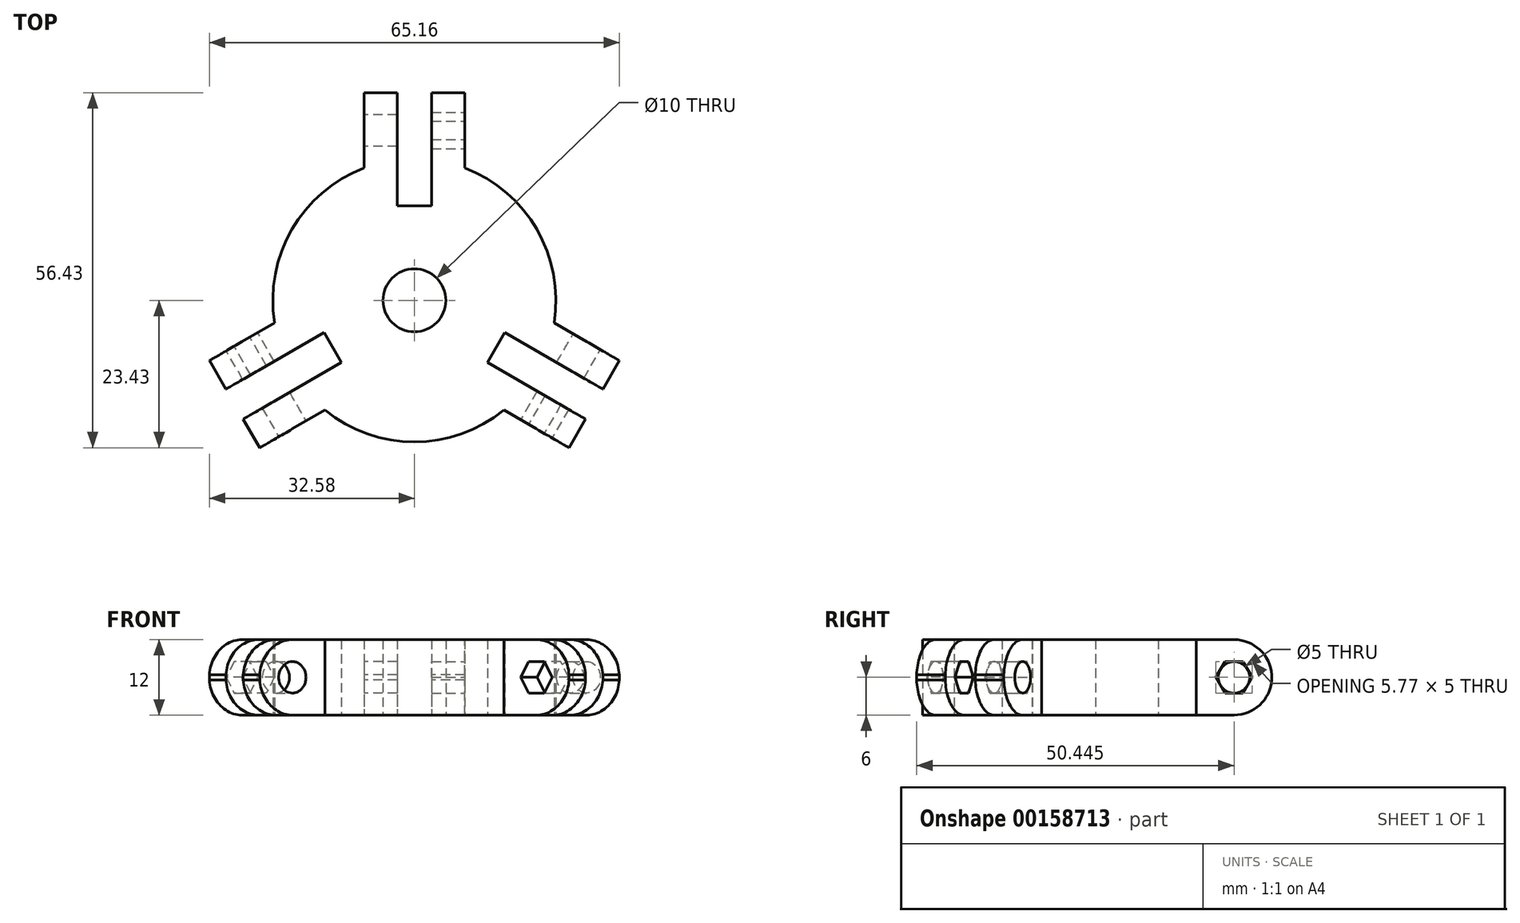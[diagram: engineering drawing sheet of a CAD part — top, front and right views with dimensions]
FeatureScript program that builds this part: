
annotation { "Feature Type Name" : "Feature", "Feature Type Description" : "" }
export const myFeature = defineFeature(function(context is Context, id is Id, definition is map)
    precondition{}
    {
        {
            var Q0;
            Q0=qCreatedBy(makeId("Top.planeOp"),FACE);
            var sketch = newSketch(context, id + "F0", { "sketchPlane" : qUnion([Q0])});
            skCircle(sketch, "E0", {"center": v(0, 0) * mm, "radius": 5 * mm});
            skLineSegment(sketch, "E1", {"start": v(0, 15) * mm, "end": v(2.75, 15) * mm});
            skLineSegment(sketch, "E2", {"start": v(2.75, 15) * mm, "end": v(2.75, 33) * mm});
            skLineSegment(sketch, "E3", {"start": v(2.75, 33) * mm, "end": v(8, 33) * mm});
            skLineSegment(sketch, "E4", {"start": v(0, 15) * mm, "end": v(-2.75, 15) * mm});
            skLineSegment(sketch, "E5", {"start": v(-2.75, 15) * mm, "end": v(-2.75, 33) * mm});
            skLineSegment(sketch, "E6", {"start": v(-2.75, 33) * mm, "end": v(-8, 33) * mm});
            skLineSegment(sketch, "E7", {"start": v(0, 0) * mm, "end": v(13, -7.5) * mm});
            skLineSegment(sketch, "E8", {"start": v(0, 0) * mm, "end": v(-13, -7.5) * mm});
            skLineSegment(sketch, "E9", {"start": v(-13, -7.5) * mm, "end": v(-14.37, -5.12) * mm});
            skLineSegment(sketch, "E10", {"start": v(-14.37, -5.12) * mm, "end": v(-29.95, -14.12) * mm});
            skLineSegment(sketch, "E11", {"start": v(-29.95, -14.12) * mm, "end": v(-32.58, -9.57) * mm});
            skLineSegment(sketch, "E12", {"start": v(-13, -7.5) * mm, "end": v(-11.62, -9.88) * mm});
            skLineSegment(sketch, "E13", {"start": v(-11.62, -9.88) * mm, "end": v(-27.2, -18.88) * mm});
            skLineSegment(sketch, "E14", {"start": v(-27.2, -18.88) * mm, "end": v(-24.58, -23.43) * mm});
            skLineSegment(sketch, "E15", {"start": v(13, -7.5) * mm, "end": v(14.37, -5.12) * mm});
            skLineSegment(sketch, "E16", {"start": v(14.37, -5.12) * mm, "end": v(29.95, -14.12) * mm});
            skLineSegment(sketch, "E17", {"start": v(29.95, -14.12) * mm, "end": v(32.58, -9.57) * mm});
            skLineSegment(sketch, "E18", {"start": v(13, -7.5) * mm, "end": v(11.62, -9.88) * mm});
            skLineSegment(sketch, "E19", {"start": v(11.62, -9.88) * mm, "end": v(27.2, -18.88) * mm});
            skLineSegment(sketch, "E20", {"start": v(27.2, -18.88) * mm, "end": v(24.58, -23.43) * mm});
            skPoint(sketch, "E21.endSnap0", {"position": v(5.37, 33) * mm});
            skArc(sketch, "E22", {"start": v(-8, 21.03) * mm, "mid": v(-19.49, 11.25) * mm, "end": v(-22.21, -3.59) * mm});
            skArc(sketch, "E23", {"start": v(8, 21.03) * mm, "mid": v(19.49, 11.25) * mm, "end": v(22.21, -3.59) * mm});
            skArc(sketch, "E24", {"start": v(-14.21, -17.44) * mm, "mid": v(0, -22.5) * mm, "end": v(14.21, -17.44) * mm});
            skLineSegment(sketch, "E25", {"start": v(-14.21, -17.44) * mm, "end": v(-24.58, -23.43) * mm});
            skLineSegment(sketch, "E26", {"start": v(-22.21, -3.59) * mm, "end": v(-32.58, -9.57) * mm});
            skLineSegment(sketch, "E27", {"start": v(-8, 21.03) * mm, "end": v(-8, 33) * mm});
            skLineSegment(sketch, "E28", {"start": v(8, 33) * mm, "end": v(8, 21.03) * mm});
            skLineSegment(sketch, "E29", {"start": v(22.21, -3.59) * mm, "end": v(32.58, -9.57) * mm});
            skLineSegment(sketch, "E30", {"start": v(24.58, -23.43) * mm, "end": v(14.21, -17.44) * mm});
            skLineSegment(sketch, "E31", {"start": v(0, 15) * mm, "end": v(0, 0) * mm});
            skSolve(sketch);
        }
        {
            var Q0;
            Q0 = qSketchRegion(id + "F0", true);
            var Q1;
            {var subQ6=sQuery(id+"F0.wireOp",EDGE,"E4");Q1=makeQuery(id+"F0.imprint","IMPRINT",FACE,{"disambiguationData":[TD([[makeQuery(id+"F0.imprint","IMPRINT",EDGE,{"derivedFrom":subQ6}),1.0]])]});}
            var Q2;
            {var subQ1=sQuery(id+"F0.wireOp",EDGE,"E1");Q2=makeQuery(id+"F0.imprint","IMPRINT",FACE,{"disambiguationData":[TD([[makeQuery(id+"F0.imprint","IMPRINT",EDGE,{"derivedFrom":subQ1}),-1.0]])]});}
            var Q3;
            {var subQ6=sQuery(id+"F0.wireOp",EDGE,"E12");Q3=makeQuery(id+"F0.imprint","IMPRINT",FACE,{"disambiguationData":[TD([[makeQuery(id+"F0.imprint","IMPRINT",EDGE,{"derivedFrom":subQ6}),1.0]])]});}
            extrude(context, id + "F1", {"entities" : qUnion([Q0, Q1, Q2, Q3]), "depth" : 12 * mm});
        }
        {
            var Q0;
            Q0=makeQuery(id+"F1.opExtrude","SWEPT_FACE",FACE,{"disambiguationData":[OSD([sQuery(id+"F0.wireOp",EDGE,"E27")])]});
            var sketch = newSketch(context, id + "F2", { "sketchPlane" : qUnion([Q0])});
            skArc(sketch, "E32", {"start": v(-27.01, 12) * mm, "mid": v(-33.01, 6) * mm, "end": v(-27.01, 0) * mm});
            skPoint(sketch, "E32.centerSnap0", {"position": v(-33, 6) * mm});
            skPoint(sketch, "E32.centerSnap1", {"position": v(-27.01, 12) * mm});
            skLineSegment(sketch, "E33", {"start": v(-27.01, 0) * mm, "end": v(-33, 0) * mm});
            skLineSegment(sketch, "E34", {"start": v(-33, 0) * mm, "end": v(-33, 12) * mm});
            skLineSegment(sketch, "E35", {"start": v(-33, 12) * mm, "end": v(-27.01, 12) * mm});
            skSolve(sketch);
        }
        {
            var Q0;
            Q0 = qSketchRegion(id + "F2", true);
            extrude(context, id + "F3", {"entities" : qUnion([Q0]), "operationType" : NewBodyOperationType.REMOVE, "oppositeDirection" : true, "depth" : 25 * mm});
        }
        {
            var Q0;
            Q0=makeQuery(id+"F1.opExtrude","SWEPT_FACE",FACE,{"disambiguationData":[OSD([sQuery(id+"F0.wireOp",EDGE,"E26")])]});
            var sketch = newSketch(context, id + "F4", { "sketchPlane" : qUnion([Q0])});
            skArc(sketch, "E36", {"start": v(27.01, 12) * mm, "mid": v(33.01, 6) * mm, "end": v(27.01, 0) * mm});
            skPoint(sketch, "E36.centerSnap0", {"position": v(27.01, 12) * mm});
            skPoint(sketch, "E36.centerSnap1", {"position": v(33, 6) * mm});
            skLineSegment(sketch, "E37", {"start": v(27.01, 12) * mm, "end": v(33, 12) * mm});
            skLineSegment(sketch, "E38", {"start": v(33, 12) * mm, "end": v(33, 0) * mm});
            skLineSegment(sketch, "E39", {"start": v(33, 0) * mm, "end": v(27.01, 0) * mm});
            skSolve(sketch);
        }
        {
            var Q0;
            Q0 = qSketchRegion(id + "F4", true);
            extrude(context, id + "F5", {"entities" : qUnion([Q0]), "operationType" : NewBodyOperationType.REMOVE, "oppositeDirection" : true, "depth" : 25 * mm});
        }
        {
            var Q0;
            Q0=makeQuery(id+"F1.opExtrude","SWEPT_FACE",FACE,{"disambiguationData":[OSD([sQuery(id+"F0.wireOp",EDGE,"E30")])]});
            var sketch = newSketch(context, id + "F6", { "sketchPlane" : qUnion([Q0])});
            skArc(sketch, "E40", {"start": v(27.01, 12) * mm, "mid": v(33.01, 6) * mm, "end": v(27.01, 0) * mm});
            skPoint(sketch, "E40.centerSnap0", {"position": v(27.01, 12) * mm});
            skPoint(sketch, "E40.centerSnap1", {"position": v(33, 6) * mm});
            skLineSegment(sketch, "E41", {"start": v(27.01, 12) * mm, "end": v(33, 12) * mm});
            skLineSegment(sketch, "E42", {"start": v(33, 12) * mm, "end": v(33, 0) * mm});
            skLineSegment(sketch, "E43", {"start": v(33, 0) * mm, "end": v(27.01, 0) * mm});
            skSolve(sketch);
        }
        {
            var Q0;
            Q0 = qSketchRegion(id + "F6", true);
            extrude(context, id + "F7", {"entities" : qUnion([Q0]), "operationType" : NewBodyOperationType.REMOVE, "oppositeDirection" : true, "depth" : 25 * mm});
        }
        {
            var Q0;
            Q0=makeQuery(id+"F1.opExtrude","SWEPT_FACE",FACE,{"disambiguationData":[OSD([sQuery(id+"F0.wireOp",EDGE,"E25")])]});
            var sketch = newSketch(context, id + "F8", { "sketchPlane" : qUnion([Q0])});
            skCircle(sketch, "E44", {"center": v(-27.01, 6) * mm, "radius": 2.5 * mm});
            skSolve(sketch);
        }
        {
            var Q0;
            Q0 = qSketchRegion(id + "F8", true);
            extrude(context, id + "F9", {"entities" : qUnion([Q0]), "operationType" : NewBodyOperationType.REMOVE, "oppositeDirection" : true, "depth" : 5.6 * mm});
        }
        {
            var Q0;
            Q0=makeQuery(id+"F1.opExtrude","SWEPT_FACE",FACE,{"disambiguationData":[OSD([sQuery(id+"F0.wireOp",EDGE,"E26")])]});
            var sketch = newSketch(context, id + "F10", { "sketchPlane" : qUnion([Q0])});
            skCircle(sketch, "E45.cCircle", {"center": v(27.01, 6) * mm, "radius": 2.5 * mm, "construction": true});
            skLineSegment(sketch, "E45.0", {"start": v(25.57, 8.5) * mm, "end": v(28.46, 8.5) * mm});
            skLineSegment(sketch, "E45.1", {"start": v(28.46, 8.5) * mm, "end": v(29.9, 6) * mm});
            skLineSegment(sketch, "E45.2", {"start": v(29.9, 6) * mm, "end": v(28.46, 3.5) * mm});
            skLineSegment(sketch, "E45.3", {"start": v(28.46, 3.5) * mm, "end": v(25.57, 3.5) * mm});
            skLineSegment(sketch, "E45.4", {"start": v(25.57, 3.5) * mm, "end": v(24.13, 6) * mm});
            skLineSegment(sketch, "E45.5", {"start": v(24.13, 6) * mm, "end": v(25.57, 8.5) * mm});
            skPoint(sketch, "E45.0.midPoint", {"position": v(27.01, 8.5) * mm});
            skSolve(sketch);
        }
        {
            var Q0;
            Q0 = qSketchRegion(id + "F10", true);
            extrude(context, id + "F11", {"entities" : qUnion([Q0]), "operationType" : NewBodyOperationType.REMOVE, "oppositeDirection" : true, "depth" : 7 * mm});
        }
        {
            var Q0;
            Q0=makeQuery(id+"F1.opExtrude","SWEPT_FACE",FACE,{"disambiguationData":[OSD([sQuery(id+"F0.wireOp",EDGE,"E27")])]});
            var sketch = newSketch(context, id + "F12", { "sketchPlane" : qUnion([Q0])});
            skCircle(sketch, "E46", {"center": v(-27.01, 6) * mm, "radius": 2.5 * mm});
            skSolve(sketch);
        }
        {
            var Q0;
            Q0 = qSketchRegion(id + "F12", true);
            extrude(context, id + "F13", {"entities" : qUnion([Q0]), "operationType" : NewBodyOperationType.REMOVE, "oppositeDirection" : true, "depth" : 7 * mm});
        }
        {
            var Q0;
            Q0=makeQuery(id+"F1.opExtrude","SWEPT_FACE",FACE,{"disambiguationData":[OSD([sQuery(id+"F0.wireOp",EDGE,"E28")])]});
            var sketch = newSketch(context, id + "F14", { "sketchPlane" : qUnion([Q0])});
            skCircle(sketch, "E47.cCircle", {"center": v(27.01, 6) * mm, "radius": 2.5 * mm, "construction": true});
            skLineSegment(sketch, "E47.0", {"start": v(25.57, 8.5) * mm, "end": v(28.46, 8.5) * mm});
            skLineSegment(sketch, "E47.1", {"start": v(28.46, 8.5) * mm, "end": v(29.9, 6) * mm});
            skLineSegment(sketch, "E47.2", {"start": v(29.9, 6) * mm, "end": v(28.46, 3.5) * mm});
            skLineSegment(sketch, "E47.3", {"start": v(28.46, 3.5) * mm, "end": v(25.57, 3.5) * mm});
            skLineSegment(sketch, "E47.4", {"start": v(25.57, 3.5) * mm, "end": v(24.13, 6) * mm});
            skLineSegment(sketch, "E47.5", {"start": v(24.13, 6) * mm, "end": v(25.57, 8.5) * mm});
            skPoint(sketch, "E47.0.midPoint", {"position": v(27.01, 8.5) * mm});
            skSolve(sketch);
        }
        {
            var Q0;
            Q0=makeQuery(id+"F14.imprint","IMPRINT",FACE,{"disambiguationData":[TD([[makeQuery(id+"F14.imprint","IMPRINT",EDGE,{"derivedFrom":sQuery(id+"F14.wireOp",EDGE,"E47.0")}),-1.0]])]});
            extrude(context, id + "F15", {"entities" : qUnion([Q0]), "operationType" : NewBodyOperationType.REMOVE, "oppositeDirection" : true, "depth" : 7 * mm});
        }
        {
            var Q0;
            Q0=makeQuery(id+"F1.opExtrude","SWEPT_FACE",FACE,{"disambiguationData":[OSD([sQuery(id+"F0.wireOp",EDGE,"E29")])]});
            var sketch = newSketch(context, id + "F16", { "sketchPlane" : qUnion([Q0])});
            skCircle(sketch, "E48", {"center": v(-27.01, 6) * mm, "radius": 2.5 * mm});
            skSolve(sketch);
        }
        {
            var Q0;
            Q0 = qSketchRegion(id + "F16", true);
            extrude(context, id + "F17", {"entities" : qUnion([Q0]), "operationType" : NewBodyOperationType.REMOVE, "oppositeDirection" : true, "depth" : 7 * mm});
        }
        {
            var Q0;
            Q0=makeQuery(id+"F1.opExtrude","SWEPT_FACE",FACE,{"disambiguationData":[OSD([sQuery(id+"F0.wireOp",EDGE,"E30")])]});
            var sketch = newSketch(context, id + "F18", { "sketchPlane" : qUnion([Q0])});
            skCircle(sketch, "E49.cCircle", {"center": v(27.01, 6) * mm, "radius": 2.5 * mm, "construction": true});
            skLineSegment(sketch, "E49.0", {"start": v(25.57, 8.5) * mm, "end": v(28.46, 8.5) * mm});
            skLineSegment(sketch, "E49.1", {"start": v(28.46, 8.5) * mm, "end": v(29.9, 6) * mm});
            skLineSegment(sketch, "E49.2", {"start": v(29.9, 6) * mm, "end": v(28.46, 3.5) * mm});
            skLineSegment(sketch, "E49.3", {"start": v(28.46, 3.5) * mm, "end": v(25.57, 3.5) * mm});
            skLineSegment(sketch, "E49.4", {"start": v(25.57, 3.5) * mm, "end": v(24.13, 6) * mm});
            skLineSegment(sketch, "E49.5", {"start": v(24.13, 6) * mm, "end": v(25.57, 8.5) * mm});
            skPoint(sketch, "E49.0.midPoint", {"position": v(27.01, 8.5) * mm});
            skSolve(sketch);
        }
        {
            var Q0;
            Q0 = qSketchRegion(id + "F18", true);
            extrude(context, id + "F19", {"entities" : qUnion([Q0]), "operationType" : NewBodyOperationType.REMOVE, "oppositeDirection" : true, "depth" : 7 * mm});
        }
    });
